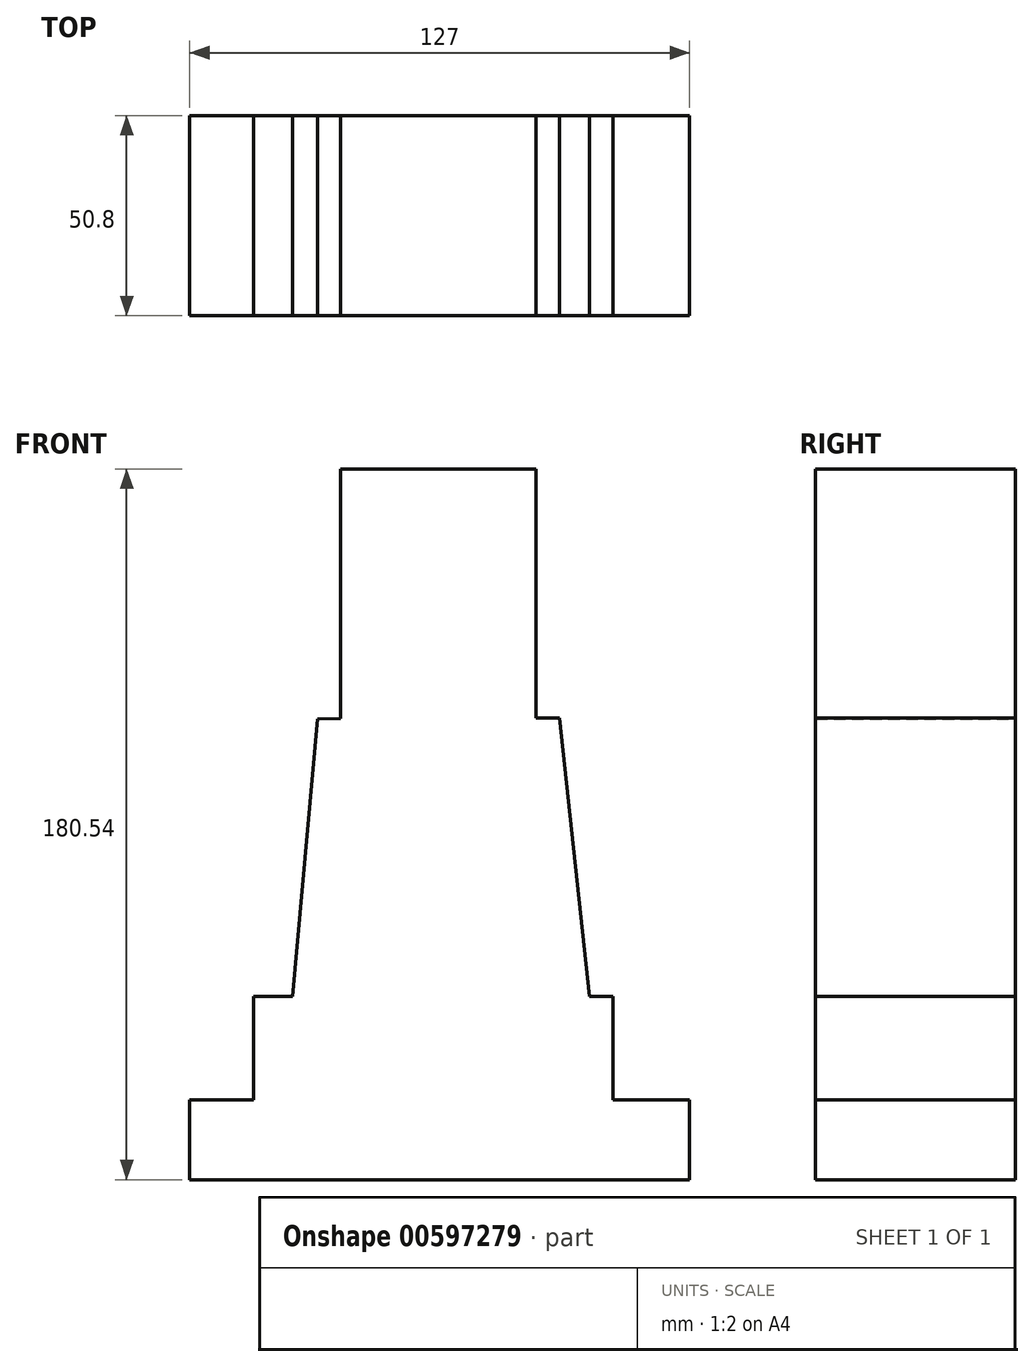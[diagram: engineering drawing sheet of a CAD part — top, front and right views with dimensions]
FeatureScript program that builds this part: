
annotation { "Feature Type Name" : "Feature", "Feature Type Description" : "" }
export const myFeature = defineFeature(function(context is Context, id is Id, definition is map)
    precondition{}
    {
        {
            var Q0;
            Q0=qCreatedBy(makeId("Front.planeOp"),FACE);
            var sketch = newSketch(context, id + "F0", { "sketchPlane" : qUnion([Q0])});
            skLineSegment(sketch, "E0.bottom", {"start": v(0, 0) * mm, "end": v(-127, 0) * mm});
            skLineSegment(sketch, "E0.top", {"start": v(0, -20.3) * mm, "end": v(-127, -20.3) * mm});
            skLineSegment(sketch, "E0.left", {"start": v(0, 0) * mm, "end": v(0, -20.3) * mm});
            skLineSegment(sketch, "E0.right", {"start": v(-127, 0) * mm, "end": v(-127, -20.3) * mm});
            skLineSegment(sketch, "E1.bottom", {"start": v(-110.83, 26.22) * mm, "end": v(-19.45, 26.22) * mm});
            skLineSegment(sketch, "E1.top", {"start": v(-110.83, 0) * mm, "end": v(-19.45, 0) * mm});
            skLineSegment(sketch, "E1.left", {"start": v(-110.83, 26.22) * mm, "end": v(-110.83, 0) * mm});
            skLineSegment(sketch, "E1.right", {"start": v(-19.45, 26.22) * mm, "end": v(-19.45, 0) * mm});
            skLineSegment(sketch, "E2", {"start": v(-100.88, 26.22) * mm, "end": v(-94.55, 96.82) * mm});
            skLineSegment(sketch, "E3", {"start": v(-33.03, 97.02) * mm, "end": v(-94.55, 96.82) * mm});
            skLineSegment(sketch, "E4", {"start": v(-33.03, 97.02) * mm, "end": v(-25.44, 26.22) * mm});
            skLineSegment(sketch, "E5.bottom", {"start": v(-88.7, 96.84) * mm, "end": v(-39.1, 96.84) * mm});
            skLineSegment(sketch, "E5.top", {"start": v(-88.7, 160.25) * mm, "end": v(-39.1, 160.25) * mm});
            skLineSegment(sketch, "E5.left", {"start": v(-88.7, 96.84) * mm, "end": v(-88.7, 160.25) * mm});
            skLineSegment(sketch, "E5.right", {"start": v(-39.1, 96.84) * mm, "end": v(-39.1, 160.25) * mm});
            skSolve(sketch);
        }
        {
            var Q0;
            Q0=makeQuery(id+"F0.imprint","IMPRINT",FACE,{"disambiguationData":[TD([[makeQuery(id+"F0.imprint","IMPRINT",EDGE,{"derivedFrom":sQuery(id+"F0.wireOp",EDGE,"E0.top")}),-1.0]])]});
            var Q1;
            Q1=makeQuery(id+"F0.imprint","IMPRINT",FACE,{"disambiguationData":[TD([[makeQuery(id+"F0.imprint","IMPRINT",EDGE,{"derivedFrom":sQuery(id+"F0.wireOp",EDGE,"E1.top")}),1.0]])]});
            var Q2;
            {var subQ4=sQuery(id+"F0.wireOp",EDGE,"E2");Q2=makeQuery(id+"F0.imprint","IMPRINT",FACE,{"disambiguationData":[TD([[makeQuery(id+"F0.imprint","IMPRINT",EDGE,{"derivedFrom":subQ4}),-1.0]])]});}
            extrude(context, id + "F1", {"entities" : qUnion([Q0, Q1, Q2]), "depth" : 25.4 * mm, "offsetDistance" : 25.4 * mm});
        }
        {
            var Q0;
            Q0=qCreatedBy(makeId("Front.planeOp"),FACE);
            var sketch = newSketch(context, id + "F2", { "sketchPlane" : qUnion([Q0])});
            skLineSegment(sketch, "E6", {"start": v(-93.28, 96.6) * mm, "end": v(-85.76, 153.53) * mm});
            skLineSegment(sketch, "E7", {"start": v(-36.03, 97.6) * mm, "end": v(-40.61, 153.86) * mm});
            skLineSegment(sketch, "E8", {"start": v(-40.61, 153.86) * mm, "end": v(-85.76, 153.86) * mm});
            skSolve(sketch);
        }
        {
            var Q0;
            Q0 = qSketchRegion(id + "F2", true);
            var Q1;
            Q1 = qConstructionFilter(qBodyType(qCreatedBy(id + "F2" ,EDGE), BodyType.WIRE), ConstructionObject.NO);
            extrude(context, id + "F3", {"entities" : qUnion([Q0]), "bodyType" : ToolBodyType.SURFACE, "surfaceEntities" : qUnion([Q1]), "depth" : 25.4 * mm, "offsetDistance" : 25.4 * mm});
        }
        {
            var Q0;
            Q0 = qSketchRegion(id + "F0", true);
            extrude(context, id + "F4", {"entities" : qUnion([Q0]), "operationType" : NewBodyOperationType.ADD, "depth" : 25.4 * mm, "offsetDistance" : 25.4 * mm});
        }
        {
            var Q0;
            Q0 = qSketchRegion(id + "F0", true);
            var Q1;
            {var subQ0=sQuery(id+"F0.wireOp",EDGE,"E5.right");var subQ1=sQuery(id+"F0.wireOp",EDGE,"E4");var subQ2=sQuery(id+"F0.wireOp",EDGE,"E3");var subQ3=sQuery(id+"F0.wireOp",EDGE,"E2");var subQ4=sQuery(id+"F0.wireOp",EDGE,"E1.right");var subQ5=sQuery(id+"F0.wireOp",EDGE,"E1.left");var subQ6=sQuery(id+"F0.wireOp",EDGE,"E1.bottom");var subQ7=sQuery(id+"F0.wireOp",EDGE,"E0.right");var subQ8=sQuery(id+"F0.wireOp",EDGE,"E0.left");var subQ9=sQuery(id+"F0.wireOp",EDGE,"E0.top");var subQ10=sQuery(id+"F0.wireOp",EDGE,"E0.bottom");Q1=makeQuery(id+"F4.boolean.opBoolean","MERGE",FACE,{"derivedFrom":[makeQuery(id+"F1.opExtrude","CAP_FACE",FACE,{"disambiguationData":[OSD([subQ10,subQ9,subQ8,subQ7,subQ6,subQ5,subQ4,subQ3,subQ2,subQ1,sQuery(id+"F0.wireOp",EDGE,"E5.bottom"),subQ0])],"isStart":false}),makeQuery(id+"F4.opExtrude","CAP_FACE",FACE,{"disambiguationData":[OSD([subQ10,subQ9,subQ8,subQ7,subQ6,subQ5,subQ4,subQ3,subQ2,subQ1,sQuery(id+"F0.wireOp",EDGE,"E5.top"),sQuery(id+"F0.wireOp",EDGE,"E5.left"),subQ0])],"isStart":false})]});}
            extrude(context, id + "F5", {"entities" : qUnion([Q0, Q1]), "operationType" : NewBodyOperationType.ADD, "depth" : 25.4 * mm, "offsetDistance" : 25.4 * mm});
        }
    });
